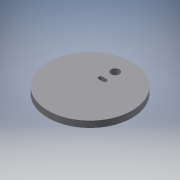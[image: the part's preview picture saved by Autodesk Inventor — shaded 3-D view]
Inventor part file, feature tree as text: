
AUTODESK INVENTOR PART (.ipt)
format: ipt  version: 2016 (Build 200138000, 138)  size: 110,592 bytes
history: native  units: mm
features: extrude x1, sketch x1
ambient origin geometry x8: Origin, YZ Plane, XZ Plane, XY Plane, X Axis, Y Axis, Z Axis, Center Point
bodies: Solid1 (feature_tree)
feature tree (2):
  extrude  "Extrusion1"  Depth=3.0mm
  sketch  "Sketch1"  dims[d0=40.0mm d1=4.0mm d2=4.0mm d3=2.0mm d4=1.0mm d5=12.0mm d6=5.0mm d7=3.0mm d8=0.0mm]
